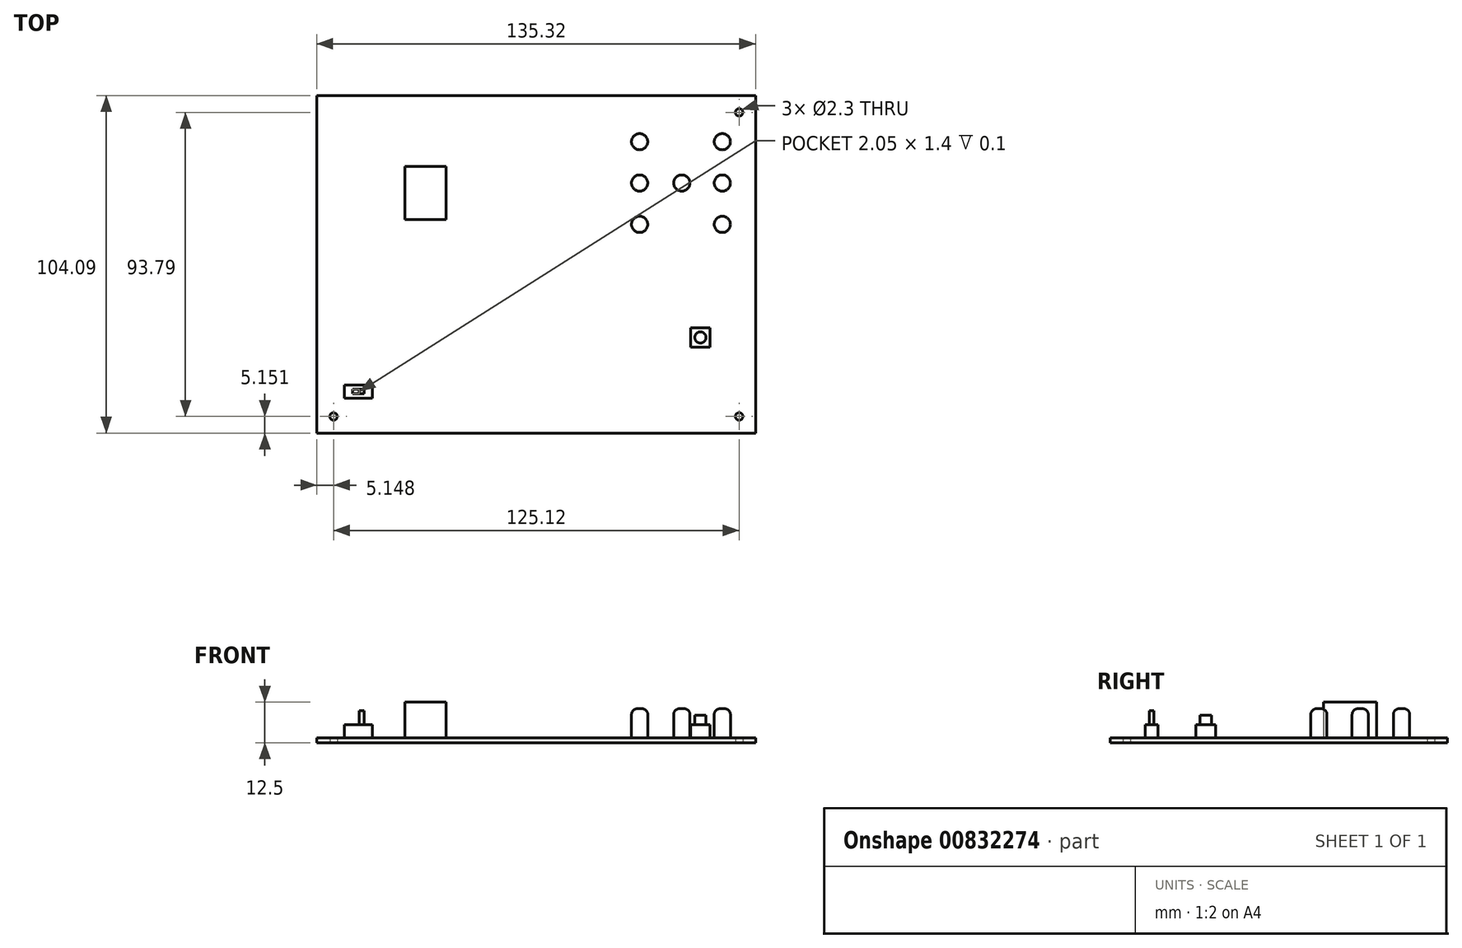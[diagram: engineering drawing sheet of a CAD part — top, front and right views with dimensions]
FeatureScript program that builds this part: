
annotation { "Feature Type Name" : "Feature", "Feature Type Description" : "" }
export const myFeature = defineFeature(function(context is Context, id is Id, definition is map)
    precondition{}
    {
        {
            var Q0;
            Q0=qCreatedBy(makeId("Top.planeOp"),FACE);
            var sketch = newSketch(context, id + "F0", { "sketchPlane" : qUnion([Q0])});
            skLineSegment(sketch, "E0.bottom", {"start": v(-61.37, 62.92) * mm, "end": v(73.95, 62.92) * mm});
            skLineSegment(sketch, "E0.top", {"start": v(-61.37, -41.17) * mm, "end": v(73.95, -41.17) * mm});
            skLineSegment(sketch, "E0.left", {"start": v(-61.37, 62.92) * mm, "end": v(-61.37, -41.17) * mm});
            skLineSegment(sketch, "E0.right", {"start": v(73.95, 62.92) * mm, "end": v(73.95, -41.17) * mm});
            skCircle(sketch, "E1", {"center": v(68.9, 57.77) * mm, "radius": 1.15 * mm});
            skCircle(sketch, "E2", {"center": v(68.9, -36.02) * mm, "radius": 1.15 * mm});
            skCircle(sketch, "E3", {"center": v(-56.22, -36.02) * mm, "radius": 1.15 * mm});
            skSolve(sketch);
        }
        {
            var Q0;
            Q0=makeQuery(id+"F0.imprint","IMPRINT",FACE,{"disambiguationData":[TD([[makeQuery(id+"F0.imprint","IMPRINT",EDGE,{"derivedFrom":sQuery(id+"F0.wireOp",EDGE,"E0.bottom")}),-1.0]])]});
            extrude(context, id + "F1", {"entities" : qUnion([Q0]), "depth" : 1.5 * mm, "offsetDistance" : 25 * mm});
        }
        {
            var Q0;
            Q0=makeQuery(id+"F1.opExtrude","CAP_FACE",FACE,{"disambiguationData":[OSD([sQuery(id+"F0.wireOp",EDGE,"E0.bottom"),sQuery(id+"F0.wireOp",EDGE,"E0.top"),sQuery(id+"F0.wireOp",EDGE,"E0.left"),sQuery(id+"F0.wireOp",EDGE,"E0.right"),sQuery(id+"F0.wireOp",EDGE,"E1"),sQuery(id+"F0.wireOp",EDGE,"E2"),sQuery(id+"F0.wireOp",EDGE,"E3")])],"isStart":false});
            var sketch = newSketch(context, id + "F2", { "sketchPlane" : qUnion([Q0])});
            skLineSegment(sketch, "E4.bottom", {"start": v(-34.22, 41.03) * mm, "end": v(-21.49, 41.03) * mm});
            skLineSegment(sketch, "E4.top", {"start": v(-34.22, 24.66) * mm, "end": v(-21.49, 24.66) * mm});
            skLineSegment(sketch, "E4.left", {"start": v(-34.22, 41.03) * mm, "end": v(-34.22, 24.66) * mm});
            skLineSegment(sketch, "E4.right", {"start": v(-21.49, 41.03) * mm, "end": v(-21.49, 24.66) * mm});
            skLineSegment(sketch, "E5.bottom", {"start": v(-52.87, -26.37) * mm, "end": v(-44.27, -26.37) * mm});
            skLineSegment(sketch, "E5.top", {"start": v(-52.87, -30.37) * mm, "end": v(-44.27, -30.37) * mm});
            skLineSegment(sketch, "E5.left", {"start": v(-52.87, -26.37) * mm, "end": v(-52.87, -30.37) * mm});
            skLineSegment(sketch, "E5.right", {"start": v(-44.27, -26.37) * mm, "end": v(-44.27, -30.37) * mm});
            skLineSegment(sketch, "E6.bottom", {"start": v(53.95, -8.67) * mm, "end": v(59.95, -8.67) * mm});
            skLineSegment(sketch, "E6.top", {"start": v(53.95, -14.67) * mm, "end": v(59.95, -14.67) * mm});
            skLineSegment(sketch, "E6.left", {"start": v(53.95, -8.67) * mm, "end": v(53.95, -14.67) * mm});
            skLineSegment(sketch, "E6.right", {"start": v(59.95, -8.67) * mm, "end": v(59.95, -14.67) * mm});
            skCircle(sketch, "E7", {"center": v(38.2, 48.72) * mm, "radius": 2.5 * mm});
            skCircle(sketch, "E8", {"center": v(38.2, 35.97) * mm, "radius": 2.5 * mm});
            skCircle(sketch, "E9", {"center": v(38.2, 23.22) * mm, "radius": 2.5 * mm});
            skCircle(sketch, "E10", {"center": v(51.2, 35.97) * mm, "radius": 2.5 * mm});
            skCircle(sketch, "E11", {"center": v(63.7, 48.72) * mm, "radius": 2.5 * mm});
            skCircle(sketch, "E12", {"center": v(63.7, 35.97) * mm, "radius": 2.5 * mm});
            skCircle(sketch, "E13", {"center": v(63.7, 23.22) * mm, "radius": 2.5 * mm});
            skLineSegment(sketch, "E14.bottom", {"start": v(-46.82, -29.07) * mm, "end": v(-50.32, -29.07) * mm});
            skLineSegment(sketch, "E14.top", {"start": v(-46.82, -27.67) * mm, "end": v(-50.32, -27.67) * mm});
            skLineSegment(sketch, "E14.left", {"start": v(-46.82, -29.07) * mm, "end": v(-46.82, -27.67) * mm});
            skLineSegment(sketch, "E14.right", {"start": v(-50.32, -29.07) * mm, "end": v(-50.32, -27.67) * mm});
            skPoint(sketch, "E14.middle", {"position": v(-48.57, -28.37) * mm});
            skPoint(sketch, "E14.middle.positionSnap0", {"position": v(-48.57, -26.37) * mm});
            skPoint(sketch, "E14.middle.positionSnap1", {"position": v(-52.87, -28.37) * mm});
            skPoint(sketch, "E14.centerSnap0", {"position": v(-48.57, -26.37) * mm});
            skPoint(sketch, "E14.centerSnap1", {"position": v(-52.87, -28.37) * mm});
            skCircle(sketch, "E15", {"center": v(56.95, -11.67) * mm, "radius": 1.74 * mm});
            skPoint(sketch, "E15.centerSnap0", {"position": v(56.95, -8.67) * mm});
            skPoint(sketch, "E15.centerSnap1", {"position": v(59.95, -11.67) * mm});
            skSolve(sketch);
        }
        {
            var Q0;
            Q0=makeQuery(id+"F2.imprint","IMPRINT",FACE,{"disambiguationData":[TD([[makeQuery(id+"F2.imprint","IMPRINT",EDGE,{"derivedFrom":sQuery(id+"F2.wireOp",EDGE,"E5.bottom")}),-1.0]])]});
            extrude(context, id + "F3", {"entities" : qUnion([Q0]), "operationType" : NewBodyOperationType.ADD, "depth" : 4 * mm, "offsetDistance" : 25 * mm});
        }
        {
            var Q0;
            Q0=makeQuery(id+"F3.boolean.opBoolean","SPLIT",FACE,{"disambiguationData":[TD([makeQuery(id+"F3.opExtrude","SWEPT_FACE",FACE,{"disambiguationData":[OSD([sQuery(id+"F2.wireOp",EDGE,"E14.bottom")])]})])],"derivedFrom":makeQuery(id+"F1.opExtrude","CAP_FACE",FACE,{"disambiguationData":[OSD([sQuery(id+"F0.wireOp",EDGE,"E0.bottom"),sQuery(id+"F0.wireOp",EDGE,"E0.top"),sQuery(id+"F0.wireOp",EDGE,"E0.left"),sQuery(id+"F0.wireOp",EDGE,"E0.right"),sQuery(id+"F0.wireOp",EDGE,"E1"),sQuery(id+"F0.wireOp",EDGE,"E2"),sQuery(id+"F0.wireOp",EDGE,"E3")])],"isStart":false})});
            extrude(context, id + "F4", {"entities" : qUnion([Q0]), "operationType" : NewBodyOperationType.ADD, "depth" : 3.9 * mm, "offsetDistance" : 25 * mm});
        }
        {
            var Q0;
            Q0=makeQuery(id+"F4.opExtrude","CAP_FACE",FACE,{"disambiguationData":[OSD([sQuery(id+"F0.wireOp",EDGE,"E0.bottom"),sQuery(id+"F0.wireOp",EDGE,"E0.top"),sQuery(id+"F0.wireOp",EDGE,"E0.left"),sQuery(id+"F0.wireOp",EDGE,"E0.right"),sQuery(id+"F0.wireOp",EDGE,"E1"),sQuery(id+"F0.wireOp",EDGE,"E2"),sQuery(id+"F0.wireOp",EDGE,"E3")])],"isStart":false});
            var sketch = newSketch(context, id + "F5", { "sketchPlane" : qUnion([Q0])});
            skLineSegment(sketch, "E16.bottom", {"start": v(-46.82, -29.07) * mm, "end": v(-48.27, -29.07) * mm});
            skLineSegment(sketch, "E16.top", {"start": v(-46.82, -27.67) * mm, "end": v(-48.27, -27.67) * mm});
            skLineSegment(sketch, "E16.left", {"start": v(-46.82, -29.07) * mm, "end": v(-46.82, -27.67) * mm});
            skLineSegment(sketch, "E16.right", {"start": v(-48.27, -29.07) * mm, "end": v(-48.27, -27.67) * mm});
            skPoint(sketch, "E16.middle", {"position": v(-47.55, -28.37) * mm});
            skPoint(sketch, "E16.middle.positionSnap0", {"position": v(-46.82, -28.37) * mm});
            skPoint(sketch, "E16.centerSnap0", {"position": v(-46.82, -28.37) * mm});
            skSolve(sketch);
        }
        {
            var Q0;
            Q0=makeQuery(id+"F5.imprint","IMPRINT",FACE,{"disambiguationData":[TD([[makeQuery(id+"F5.imprint","IMPRINT",EDGE,{"derivedFrom":sQuery(id+"F5.wireOp",EDGE,"E16.bottom")}),-1.0]])]});
            extrude(context, id + "F6", {"entities" : qUnion([Q0]), "operationType" : NewBodyOperationType.ADD, "depth" : 4.5 * mm, "offsetDistance" : 25 * mm});
        }
        {
            var Q0;
            Q0=makeQuery(id+"F2.imprint","IMPRINT",FACE,{"disambiguationData":[TD([[makeQuery(id+"F2.imprint","IMPRINT",EDGE,{"derivedFrom":sQuery(id+"F2.wireOp",EDGE,"E6.bottom")}),-1.0]])]});
            extrude(context, id + "F7", {"entities" : qUnion([Q0]), "operationType" : NewBodyOperationType.ADD, "depth" : 4 * mm, "offsetDistance" : 25 * mm});
        }
        {
            var Q0;
            Q0=makeQuery(id+"F2.imprint","IMPRINT",FACE,{"disambiguationData":[TD([[makeQuery(id+"F2.imprint","IMPRINT",EDGE,{"derivedFrom":sQuery(id+"F2.wireOp",EDGE,"E15")}),1.0]])]});
            extrude(context, id + "F8", {"entities" : qUnion([Q0]), "operationType" : NewBodyOperationType.ADD, "depth" : 7 * mm, "offsetDistance" : 25 * mm});
        }
        {
            var Q0;
            Q0=makeQuery(id+"F2.imprint","IMPRINT",FACE,{"disambiguationData":[TD([[makeQuery(id+"F2.imprint","IMPRINT",EDGE,{"derivedFrom":sQuery(id+"F2.wireOp",EDGE,"E9")}),1.0]])]});
            var Q1;
            Q1=makeQuery(id+"F2.imprint","IMPRINT",FACE,{"disambiguationData":[TD([[makeQuery(id+"F2.imprint","IMPRINT",EDGE,{"derivedFrom":sQuery(id+"F2.wireOp",EDGE,"E10")}),1.0]])]});
            var Q2;
            Q2=makeQuery(id+"F2.imprint","IMPRINT",FACE,{"disambiguationData":[TD([[makeQuery(id+"F2.imprint","IMPRINT",EDGE,{"derivedFrom":sQuery(id+"F2.wireOp",EDGE,"E12")}),1.0]])]});
            var Q3;
            Q3=makeQuery(id+"F2.imprint","IMPRINT",FACE,{"disambiguationData":[TD([[makeQuery(id+"F2.imprint","IMPRINT",EDGE,{"derivedFrom":sQuery(id+"F2.wireOp",EDGE,"E13")}),1.0]])]});
            var Q4;
            Q4=makeQuery(id+"F2.imprint","IMPRINT",FACE,{"disambiguationData":[TD([[makeQuery(id+"F2.imprint","IMPRINT",EDGE,{"derivedFrom":sQuery(id+"F2.wireOp",EDGE,"E8")}),1.0]])]});
            var Q5;
            Q5=makeQuery(id+"F2.imprint","IMPRINT",FACE,{"disambiguationData":[TD([[makeQuery(id+"F2.imprint","IMPRINT",EDGE,{"derivedFrom":sQuery(id+"F2.wireOp",EDGE,"E11")}),1.0]])]});
            var Q6;
            Q6=makeQuery(id+"F2.imprint","IMPRINT",FACE,{"disambiguationData":[TD([[makeQuery(id+"F2.imprint","IMPRINT",EDGE,{"derivedFrom":sQuery(id+"F2.wireOp",EDGE,"E7")}),1.0]])]});
            extrude(context, id + "F9", {"entities" : qUnion([Q0, Q1, Q2, Q3, Q4, Q5, Q6]), "operationType" : NewBodyOperationType.ADD, "depth" : 9 * mm, "offsetDistance" : 25 * mm});
        }
        {
            var Q0;
            Q0=makeQuery(id+"F9.opExtrude","CAP_EDGE",EDGE,{"disambiguationData":[OSD([sQuery(id+"F2.wireOp",EDGE,"E9")])],"isStart":false});
            var Q1;
            Q1=makeQuery(id+"F9.opExtrude","CAP_EDGE",EDGE,{"disambiguationData":[OSD([sQuery(id+"F2.wireOp",EDGE,"E8")])],"isStart":false});
            var Q2;
            Q2=makeQuery(id+"F9.opExtrude","CAP_EDGE",EDGE,{"disambiguationData":[OSD([sQuery(id+"F2.wireOp",EDGE,"E10")])],"isStart":false});
            var Q3;
            Q3=makeQuery(id+"F9.opExtrude","CAP_EDGE",EDGE,{"disambiguationData":[OSD([sQuery(id+"F2.wireOp",EDGE,"E7")])],"isStart":false});
            var Q4;
            Q4=makeQuery(id+"F9.opExtrude","CAP_EDGE",EDGE,{"disambiguationData":[OSD([sQuery(id+"F2.wireOp",EDGE,"E12")])],"isStart":false});
            var Q5;
            Q5=makeQuery(id+"F9.opExtrude","CAP_EDGE",EDGE,{"disambiguationData":[OSD([sQuery(id+"F2.wireOp",EDGE,"E11")])],"isStart":false});
            var Q6;
            Q6=makeQuery(id+"F9.opExtrude","CAP_EDGE",EDGE,{"disambiguationData":[OSD([sQuery(id+"F2.wireOp",EDGE,"E13")])],"isStart":false});
            fillet(context, id + "F10", {"entities" : qUnion([Q0, Q1, Q2, Q3, Q4, Q5, Q6]), "radius" : 1.8 * mm, "tangentPropagation" : true, "allowEdgeOverflow" : false});
        }
        {
            var Q0;
            Q0=makeQuery(id+"F2.imprint","IMPRINT",FACE,{"disambiguationData":[TD([[makeQuery(id+"F2.imprint","IMPRINT",EDGE,{"derivedFrom":sQuery(id+"F2.wireOp",EDGE,"E4.bottom")}),-1.0]])]});
            extrude(context, id + "F11", {"entities" : qUnion([Q0]), "operationType" : NewBodyOperationType.ADD, "depth" : 11 * mm, "offsetDistance" : 25 * mm});
        }
    });
